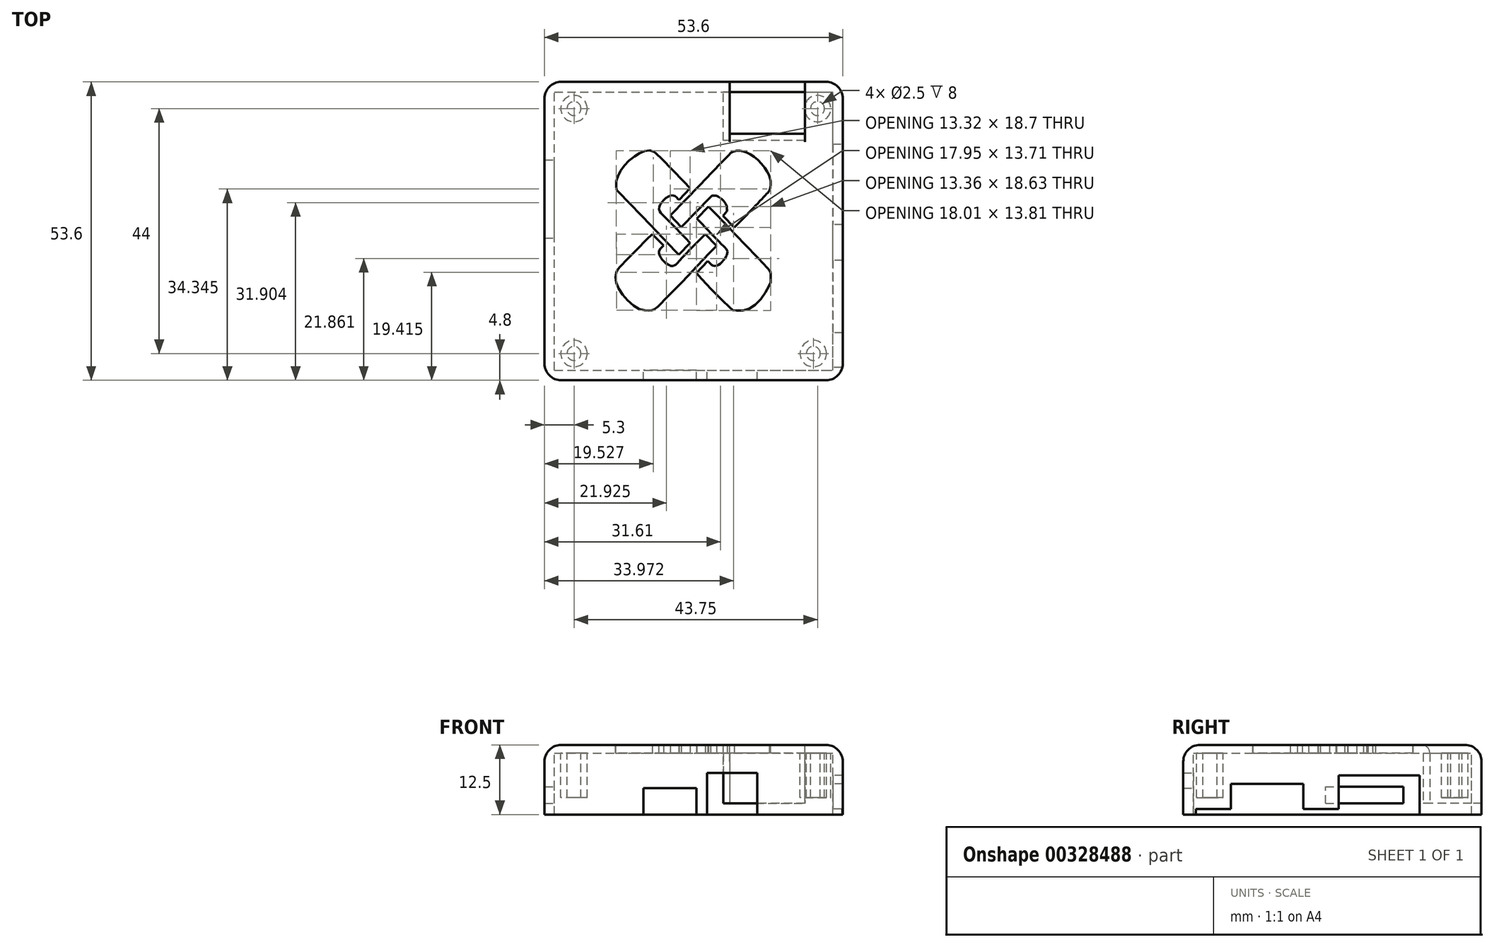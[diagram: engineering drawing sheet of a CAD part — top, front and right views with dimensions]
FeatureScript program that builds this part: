
annotation { "Feature Type Name" : "Feature", "Feature Type Description" : "" }
export const myFeature = defineFeature(function(context is Context, id is Id, definition is map)
    precondition{}
    {
        {
            var Q0;
            Q0=qCreatedBy(makeId("Top.planeOp"),FACE);
            var sketch = newSketch(context, id + "F0", { "sketchPlane" : qUnion([Q0])});
            skPoint(sketch, "E0.middle", {"position": v(0, 0) * mm});
            skLineSegment(sketch, "E1.bottom", {"start": v(-25, -25) * mm, "end": v(25, -25) * mm});
            skLineSegment(sketch, "E1.top", {"start": v(-25, 25) * mm, "end": v(25, 25) * mm});
            skLineSegment(sketch, "E1.left", {"start": v(-25, -25) * mm, "end": v(-25, 25) * mm});
            skLineSegment(sketch, "E1.right", {"start": v(25, -25) * mm, "end": v(25, 25) * mm});
            skLineSegment(sketch, "E2.0", {"start": v(-26.8, 26.8) * mm, "end": v(26.8, 26.8) * mm});
            skLineSegment(sketch, "E2.1", {"start": v(-26.8, -26.8) * mm, "end": v(-26.8, 26.8) * mm});
            skLineSegment(sketch, "E2.2", {"start": v(-26.8, -26.8) * mm, "end": v(26.8, -26.8) * mm});
            skLineSegment(sketch, "E2.3", {"start": v(26.8, -26.8) * mm, "end": v(26.8, 26.8) * mm});
            skLineSegment(sketch, "E3.bottom", {"start": v(-21.5, -22) * mm, "end": v(21.5, -22) * mm, "construction": true});
            skLineSegment(sketch, "E3.top", {"start": v(-21.5, 22) * mm, "end": v(21.5, 22) * mm, "construction": true});
            skLineSegment(sketch, "E3.left", {"start": v(-21.5, -22) * mm, "end": v(-21.5, 22) * mm, "construction": true});
            skLineSegment(sketch, "E3.right", {"start": v(21.5, -22) * mm, "end": v(21.5, 22) * mm, "construction": true});
            skLineSegment(sketch, "E4", {"start": v(21.5, 22) * mm, "end": v(22.25, 22) * mm, "construction": true});
            skCircle(sketch, "E5", {"center": v(22.25, 22) * mm, "radius": 1.25 * mm});
            skCircle(sketch, "E6", {"center": v(-21.5, 22) * mm, "radius": 1.25 * mm});
            skCircle(sketch, "E7", {"center": v(-21.5, -22) * mm, "radius": 1.25 * mm});
            skCircle(sketch, "E8", {"center": v(21.5, -22) * mm, "radius": 1.25 * mm});
            skCircle(sketch, "E9", {"center": v(-21.5, 22) * mm, "radius": 2.38 * mm});
            skCircle(sketch, "E10", {"center": v(22.25, 22) * mm, "radius": 2.38 * mm});
            skCircle(sketch, "E11", {"center": v(21.5, -22) * mm, "radius": 2.38 * mm});
            skCircle(sketch, "E12", {"center": v(-21.5, -22) * mm, "radius": 2.38 * mm});
            skSolve(sketch);
        }
        {
            var Q0;
            Q0=makeQuery(id+"F0.imprint","IMPRINT",FACE,{"disambiguationData":[TD([[makeQuery(id+"F0.imprint","IMPRINT",EDGE,{"derivedFrom":sQuery(id+"F0.wireOp",EDGE,"E1.bottom")}),1.0]])]});
            var Q1;
            Q1=makeQuery(id+"F0.imprint","IMPRINT",FACE,{"disambiguationData":[TD([[makeQuery(id+"F0.imprint","IMPRINT",EDGE,{"derivedFrom":sQuery(id+"F0.wireOp",EDGE,"E6")}),1.0]])]});
            var Q2;
            Q2=makeQuery(id+"F0.imprint","IMPRINT",FACE,{"disambiguationData":[TD([[makeQuery(id+"F0.imprint","IMPRINT",EDGE,{"derivedFrom":sQuery(id+"F0.wireOp",EDGE,"E5")}),1.0]])]});
            var Q3;
            Q3=makeQuery(id+"F0.imprint","IMPRINT",FACE,{"disambiguationData":[TD([[makeQuery(id+"F0.imprint","IMPRINT",EDGE,{"derivedFrom":sQuery(id+"F0.wireOp",EDGE,"E8")}),1.0]])]});
            var Q4;
            Q4=makeQuery(id+"F0.imprint","IMPRINT",FACE,{"disambiguationData":[TD([[makeQuery(id+"F0.imprint","IMPRINT",EDGE,{"derivedFrom":sQuery(id+"F0.wireOp",EDGE,"E7")}),1.0]])]});
            extrude(context, id + "F1", {"entities" : qUnion([Q0, Q1, Q2, Q3, Q4]), "depth" : 1.5 * mm});
        }
        {
            var Q0;
            Q0=makeQuery(id+"F0.imprint","IMPRINT",FACE,{"disambiguationData":[TD([[makeQuery(id+"F0.imprint","IMPRINT",EDGE,{"derivedFrom":sQuery(id+"F0.wireOp",EDGE,"E6")}),-1.0]])]});
            var Q1;
            Q1=makeQuery(id+"F0.imprint","IMPRINT",FACE,{"disambiguationData":[TD([[makeQuery(id+"F0.imprint","IMPRINT",EDGE,{"derivedFrom":sQuery(id+"F0.wireOp",EDGE,"E5")}),-1.0]])]});
            var Q2;
            Q2=makeQuery(id+"F0.imprint","IMPRINT",FACE,{"disambiguationData":[TD([[makeQuery(id+"F0.imprint","IMPRINT",EDGE,{"derivedFrom":sQuery(id+"F0.wireOp",EDGE,"E8")}),-1.0]])]});
            var Q3;
            Q3=makeQuery(id+"F0.imprint","IMPRINT",FACE,{"disambiguationData":[TD([[makeQuery(id+"F0.imprint","IMPRINT",EDGE,{"derivedFrom":sQuery(id+"F0.wireOp",EDGE,"E7")}),-1.0]])]});
            var Q4;
            Q4=makeQuery(id+"F1.opExtrude","CAP_FACE",FACE,{"disambiguationData":[OSD([sQuery(id+"F0.wireOp",EDGE,"E1.bottom"),sQuery(id+"F0.wireOp",EDGE,"E1.top"),sQuery(id+"F0.wireOp",EDGE,"E1.left"),sQuery(id+"F0.wireOp",EDGE,"E1.right"),sQuery(id+"F0.wireOp",EDGE,"E9"),sQuery(id+"F0.wireOp",EDGE,"E10"),sQuery(id+"F0.wireOp",EDGE,"E11"),sQuery(id+"F0.wireOp",EDGE,"E12")])],"isStart":false});
            extrude(context, id + "F2", {"entities" : qUnion([Q0, Q1, Q2, Q3]), "operationType" : NewBodyOperationType.ADD, "oppositeDirection" : true, "depth" : 8 * mm, "hasSecondDirection" : true, "secondDirectionOppositeDirection" : false, "secondDirectionBoundEntityFace" : qUnion([Q4]), "secondDirectionDepth" : 1.5 * mm});
        }
        {
            var Q0;
            Q0=makeQuery(id+"F0.imprint","IMPRINT",FACE,{"disambiguationData":[TD([[makeQuery(id+"F0.imprint","IMPRINT",EDGE,{"derivedFrom":sQuery(id+"F0.wireOp",EDGE,"E1.bottom")}),-1.0]])]});
            extrude(context, id + "F3", {"entities" : qUnion([Q0]), "operationType" : NewBodyOperationType.ADD, "oppositeDirection" : true, "depth" : 11 * mm, "hasSecondDirection" : true, "secondDirectionOppositeDirection" : false, "secondDirectionDepth" : 1.5 * mm});
        }
        {
            var Q0;
            Q0=qCreatedBy(makeId("Front.planeOp"),FACE);
            var sketch = newSketch(context, id + "F4", { "sketchPlane" : qUnion([Q0])});
            skLineSegment(sketch, "E13", {"start": v(0, 0) * mm, "end": v(0, -10) * mm, "construction": true});
            skLineSegment(sketch, "E14", {"start": v(0, -10) * mm, "end": v(-24.5, -10) * mm, "construction": true});
            skLineSegment(sketch, "E15", {"start": v(-24.5, -10) * mm, "end": v(-24.5, -7.25) * mm, "construction": true});
            skLineSegment(sketch, "E16", {"start": v(-24.5, -7.25) * mm, "end": v(-4.25, -7.25) * mm, "construction": true});
            skLineSegment(sketch, "E17.bottom", {"start": v(-9, -8.25) * mm, "end": v(0.5, -8.25) * mm});
            skLineSegment(sketch, "E17.top", {"start": v(-9, -6.25) * mm, "end": v(0.5, -6.25) * mm});
            skLineSegment(sketch, "E17.left", {"start": v(-9, -8.25) * mm, "end": v(-9, -6.25) * mm});
            skLineSegment(sketch, "E17.right", {"start": v(0.5, -8.25) * mm, "end": v(0.5, -6.25) * mm});
            skPoint(sketch, "E17.middle", {"position": v(-4.25, -7.25) * mm});
            skLineSegment(sketch, "E18", {"start": v(-24.5, -7.25) * mm, "end": v(-24.5, -6.15) * mm, "construction": true});
            skLineSegment(sketch, "E19", {"start": v(-24.5, -6.15) * mm, "end": v(6.9, -6.15) * mm, "construction": true});
            skLineSegment(sketch, "E20.bottom", {"start": v(11.4, -8.75) * mm, "end": v(2.4, -8.75) * mm});
            skLineSegment(sketch, "E20.top", {"start": v(11.4, -3.55) * mm, "end": v(2.4, -3.55) * mm});
            skLineSegment(sketch, "E20.left", {"start": v(11.4, -8.75) * mm, "end": v(11.4, -3.55) * mm});
            skLineSegment(sketch, "E20.right", {"start": v(2.4, -8.75) * mm, "end": v(2.4, -3.55) * mm});
            skPoint(sketch, "E20.middle", {"position": v(6.9, -6.15) * mm});
            skLineSegment(sketch, "E21", {"start": v(11.4, -8.75) * mm, "end": v(11.4, -11) * mm});
            skLineSegment(sketch, "E22", {"start": v(11.4, -11) * mm, "end": v(2.4, -11) * mm});
            skLineSegment(sketch, "E23", {"start": v(2.4, -11) * mm, "end": v(2.4, -8.75) * mm});
            skLineSegment(sketch, "E24", {"start": v(0.5, -8.25) * mm, "end": v(0.5, -11) * mm});
            skLineSegment(sketch, "E25", {"start": v(0.5, -11) * mm, "end": v(-9, -11) * mm});
            skLineSegment(sketch, "E26", {"start": v(-9, -11) * mm, "end": v(-9, -8.25) * mm});
            skLineSegment(sketch, "E27", {"start": v(2.4, -11.11) * mm, "end": v(2.4, -12.2) * mm});
            skSolve(sketch);
        }
        {
            var Q0;
            Q0 = qSketchRegion(id + "F4", true);
            extrude(context, id + "F5", {"entities" : qUnion([Q0]), "operationType" : NewBodyOperationType.REMOVE, "endBound" : BoundingType.THROUGH_ALL, "depth" : 25 * mm});
        }
        {
            var Q0;
            Q0=qCreatedBy(makeId("Right.planeOp"),FACE);
            var sketch = newSketch(context, id + "F6", { "sketchPlane" : qUnion([Q0])});
            skLineSegment(sketch, "E28", {"start": v(0, 0) * mm, "end": v(0, -10) * mm, "construction": true});
            skLineSegment(sketch, "E29", {"start": v(0, -10) * mm, "end": v(-24.5, -10) * mm});
            skLineSegment(sketch, "E30", {"start": v(-24.5, -10) * mm, "end": v(-24.5, -7) * mm, "construction": true});
            skLineSegment(sketch, "E31", {"start": v(-24.5, -7) * mm, "end": v(-11.75, -7) * mm, "construction": true});
            skLineSegment(sketch, "E32.bottom", {"start": v(-18.25, -8.5) * mm, "end": v(-5.25, -8.5) * mm});
            skLineSegment(sketch, "E32.top", {"start": v(-18.25, -5.5) * mm, "end": v(-5.25, -5.5) * mm});
            skLineSegment(sketch, "E32.left", {"start": v(-18.25, -8.5) * mm, "end": v(-18.25, -5.5) * mm});
            skLineSegment(sketch, "E32.right", {"start": v(-5.25, -8.5) * mm, "end": v(-5.25, -5.5) * mm});
            skPoint(sketch, "E32.middle", {"position": v(-11.75, -7) * mm});
            skLineSegment(sketch, "E33", {"start": v(0, -10) * mm, "end": v(8.4, -10) * mm, "construction": true});
            skLineSegment(sketch, "E34", {"start": v(8.4, -10) * mm, "end": v(8.4, -7) * mm, "construction": true});
            skLineSegment(sketch, "E35.bottom", {"start": v(1.14, -10) * mm, "end": v(15.64, -10) * mm});
            skLineSegment(sketch, "E35.top", {"start": v(1.14, -4) * mm, "end": v(15.64, -4) * mm});
            skLineSegment(sketch, "E35.left", {"start": v(1.14, -10) * mm, "end": v(1.14, -4) * mm});
            skLineSegment(sketch, "E35.right", {"start": v(15.64, -10) * mm, "end": v(15.64, -4) * mm});
            skPoint(sketch, "E35.middle", {"position": v(8.4, -7) * mm});
            skLineSegment(sketch, "E36", {"start": v(-18.25, -8.5) * mm, "end": v(-18.25, -11.13) * mm});
            skLineSegment(sketch, "E37", {"start": v(-18.25, -11.13) * mm, "end": v(-5.25, -11.13) * mm});
            skLineSegment(sketch, "E38", {"start": v(-5.25, -11.13) * mm, "end": v(-5.25, -8.5) * mm});
            skLineSegment(sketch, "E39", {"start": v(1.14, -10) * mm, "end": v(1.14, -11.13) * mm});
            skLineSegment(sketch, "E40", {"start": v(1.14, -11.13) * mm, "end": v(15.64, -11.13) * mm});
            skLineSegment(sketch, "E41", {"start": v(15.64, -11.13) * mm, "end": v(15.64, -10) * mm});
            skLineSegment(sketch, "E42", {"start": v(-24.5, -10) * mm, "end": v(-24.5, -11.13) * mm});
            skLineSegment(sketch, "E43", {"start": v(-24.5, -11.13) * mm, "end": v(-18.25, -11.13) * mm});
            skLineSegment(sketch, "E44", {"start": v(0, -10) * mm, "end": v(0, -11.13) * mm});
            skLineSegment(sketch, "E45", {"start": v(0, -11.13) * mm, "end": v(-5.25, -11.13) * mm});
            skLineSegment(sketch, "E46", {"start": v(0, -10) * mm, "end": v(1.14, -10) * mm});
            skLineSegment(sketch, "E47", {"start": v(0, -11.13) * mm, "end": v(1.14, -11.13) * mm});
            skSolve(sketch);
        }
        {
            var Q0;
            Q0 = qSketchRegion(id + "F6", true);
            extrude(context, id + "F7", {"entities" : qUnion([Q0]), "operationType" : NewBodyOperationType.REMOVE, "endBound" : BoundingType.THROUGH_ALL, "depth" : 25 * mm});
        }
        {
            var Q0;
            Q0=qCreatedBy(makeId("Right.planeOp"),FACE);
            cPlane(context, id + "F8", {"entities" : qUnion([Q0]), "cplaneType" : CPlaneType.OFFSET, "offset" : 6.5 * mm, "width" : 150 * mm, "height" : 150 * mm});
        }
        {
            var Q0;
            Q0=qCreatedBy(id+"F8.planeOp",FACE);
            var sketch = newSketch(context, id + "F9", { "sketchPlane" : qUnion([Q0])});
            skLineSegment(sketch, "E48", {"start": v(0, 0) * mm, "end": v(26.8, 0) * mm, "construction": true});
            skLineSegment(sketch, "E49.bottom", {"start": v(26.8, 0) * mm, "end": v(16.3, 0) * mm});
            skLineSegment(sketch, "E49.top", {"start": v(26.8, -9) * mm, "end": v(16.3, -9) * mm});
            skLineSegment(sketch, "E49.left", {"start": v(26.8, 0) * mm, "end": v(26.8, -9) * mm});
            skLineSegment(sketch, "E49.right", {"start": v(16.3, 0) * mm, "end": v(16.3, -9) * mm});
            skLineSegment(sketch, "E50.1", {"start": v(17.5, 0) * mm, "end": v(17.5, -5.8) * mm});
            skLineSegment(sketch, "E51", {"start": v(17.5, -5.8) * mm, "end": v(17.5, -9) * mm});
            skLineSegment(sketch, "E52", {"start": v(16.3, 0) * mm, "end": v(16.3, 1.5) * mm});
            skLineSegment(sketch, "E53", {"start": v(16.3, 1.5) * mm, "end": v(26.8, 1.5) * mm});
            skLineSegment(sketch, "E54", {"start": v(26.8, 1.5) * mm, "end": v(26.8, 0) * mm});
            skLineSegment(sketch, "E55", {"start": v(17.5, 0) * mm, "end": v(17.5, 1.5) * mm});
            skSolve(sketch);
        }
        {
            var Q0;
            Q0 = qSketchRegion(id + "F9", true);
            extrude(context, id + "F10", {"entities" : qUnion([Q0]), "operationType" : NewBodyOperationType.REMOVE, "depth" : 13.5 * mm});
        }
        {
            var Q0;
            {var subQ0=sQuery(id+"F9.wireOp",EDGE,"E49.right");Q0=makeQuery(id+"F9.imprint","IMPRINT",FACE,{"disambiguationData":[TD([[makeQuery(id+"F9.imprint","IMPRINT",EDGE,{"derivedFrom":subQ0}),1.0]])]});}
            var Q1;
            {var subQ0=sQuery(id+"F9.wireOp",EDGE,"E52");Q1=makeQuery(id+"F9.imprint","IMPRINT",FACE,{"disambiguationData":[TD([[makeQuery(id+"F9.imprint","IMPRINT",EDGE,{"derivedFrom":subQ0}),-1.0]])]});}
            var Q2;
            Q2=makeQuery(id+"F3.opExtrude","SWEPT_FACE",FACE,{"disambiguationData":[OSD([sQuery(id+"F0.wireOp",EDGE,"E2.3")])]});
            extrude(context, id + "F11", {"entities" : qUnion([Q0, Q1]), "operationType" : NewBodyOperationType.ADD, "endBoundEntityFace" : qUnion([Q2]), "depth" : 13.5 * mm});
        }
        {
            var Q0;
            Q0 = qSketchRegion(id + "F9", true);
            extrude(context, id + "F12", {"entities" : qUnion([Q0]), "operationType" : NewBodyOperationType.ADD, "oppositeDirection" : true, "depth" : 1.2 * mm});
        }
        {
            var Q0;
            {var subQ6=sQuery(id+"F0.wireOp",EDGE,"E2.3");var subQ9=sQuery(id+"F0.wireOp",EDGE,"E2.0");Q0=makeQuery(id+"F10.boolean.opBoolean","SPLIT",EDGE,{"disambiguationData":[TD([makeQuery(id+"F3.opExtrude","SWEPT_FACE",FACE,{"disambiguationData":[OSD([subQ6])]})])],"derivedFrom":makeQuery(id+"F3.opExtrude","CAP_EDGE",EDGE,{"disambiguationData":[OSD([subQ9])],"isStart":true})});}
            var Q1;
            {var subQ8=sQuery(id+"F0.wireOp",EDGE,"E2.0");var subQ13=sQuery(id+"F0.wireOp",EDGE,"E2.1");Q1=makeQuery(id+"F10.boolean.opBoolean","SPLIT",EDGE,{"disambiguationData":[TD([makeQuery(id+"F3.opExtrude","SWEPT_FACE",FACE,{"disambiguationData":[OSD([subQ13])]})])],"derivedFrom":makeQuery(id+"F3.opExtrude","CAP_EDGE",EDGE,{"disambiguationData":[OSD([subQ8])],"isStart":true})});}
            var Q2;
            {var subQ4=sQuery(id+"F9.wireOp",EDGE,"E49.right");var subQ5=sQuery(id+"F9.wireOp",EDGE,"E49.left");var subQ6=sQuery(id+"F9.wireOp",EDGE,"E49.top");var subQ7=sQuery(id+"F9.wireOp",EDGE,"E49.bottom");var subQ16=sQuery(id+"F9.wireOp",EDGE,"E50.1");Q2=makeQuery(id+"F11.boolean.opBoolean","SPLIT",EDGE,{"disambiguationData":[TD([makeQuery(id+"F10.boolean.opBoolean","COPY",FACE,{"derivedFrom":makeQuery(id+"F10.opExtrude","CAP_FACE",FACE,{"disambiguationData":[OSD([subQ7,subQ6,subQ5,subQ4])],"isStart":true})})])],"derivedFrom":makeQuery(id+"F11.opExtrude","SWEPT_EDGE",EDGE,{"disambiguationData":[OSD([subQ7,subQ16])]})});}
            var Q3;
            Q3=makeQuery(id+"F10.boolean.opBoolean","COPY",EDGE,{"derivedFrom":makeQuery(id+"F10.opExtrude","CAP_EDGE",EDGE,{"disambiguationData":[OSD([sQuery(id+"F9.wireOp",EDGE,"E49.bottom")])],"isStart":true})});
            var Q4;
            Q4=makeQuery(id+"F3.opExtrude","CAP_EDGE",EDGE,{"disambiguationData":[OSD([sQuery(id+"F0.wireOp",EDGE,"E2.1")])],"isStart":true});
            var Q5;
            Q5=makeQuery(id+"F3.opExtrude","CAP_EDGE",EDGE,{"disambiguationData":[OSD([sQuery(id+"F0.wireOp",EDGE,"E2.2")])],"isStart":true});
            var Q6;
            Q6=makeQuery(id+"F3.opExtrude","SWEPT_EDGE",EDGE,{"disambiguationData":[OSD([sQuery(id+"F0.wireOp",EDGE,"E2.1"),sQuery(id+"F0.wireOp",EDGE,"E2.2")])]});
            var Q7;
            Q7=makeQuery(id+"F10.boolean.opBoolean","COPY",EDGE,{"derivedFrom":makeQuery(id+"F10.opExtrude","CAP_EDGE",EDGE,{"disambiguationData":[OSD([sQuery(id+"F9.wireOp",EDGE,"E49.left")])],"isStart":false})});
            var Q8;
            Q8=makeQuery(id+"F3.opExtrude","SWEPT_EDGE",EDGE,{"disambiguationData":[OSD([sQuery(id+"F0.wireOp",EDGE,"E2.0"),sQuery(id+"F0.wireOp",EDGE,"E2.3")])]});
            var Q9;
            {var subQ6=sQuery(id+"F0.wireOp",EDGE,"E2.3");var subQ13=sQuery(id+"F0.wireOp",EDGE,"E2.2");Q9=makeQuery(id+"F11.boolean.opBoolean","SPLIT",EDGE,{"disambiguationData":[TD([makeQuery(id+"F3.opExtrude","SWEPT_FACE",FACE,{"disambiguationData":[OSD([subQ13])]})])],"derivedFrom":makeQuery(id+"F3.opExtrude","CAP_EDGE",EDGE,{"disambiguationData":[OSD([subQ6])],"isStart":true})});}
            var Q10;
            Q10=makeQuery(id+"F3.opExtrude","SWEPT_EDGE",EDGE,{"disambiguationData":[OSD([sQuery(id+"F0.wireOp",EDGE,"E2.2"),sQuery(id+"F0.wireOp",EDGE,"E2.3")])]});
            var Q11;
            Q11=makeQuery(id+"F3.opExtrude","SWEPT_EDGE",EDGE,{"disambiguationData":[OSD([sQuery(id+"F0.wireOp",EDGE,"E2.0"),sQuery(id+"F0.wireOp",EDGE,"E2.1")])]});
            fillet(context, id + "F13", {"entities" : qUnion([Q0, Q1, Q2, Q3, Q4, Q5, Q6, Q7, Q8, Q9, Q10, Q11]), "radius" : 3 * mm, "tangentPropagation" : true, "allowEdgeOverflow" : false});
        }
        {
            var Q0;
            Q0=makeQuery(id+"F11.opExtrude","SWEPT_EDGE",EDGE,{"disambiguationData":[OSD([sQuery(id+"F9.wireOp",EDGE,"E53"),sQuery(id+"F9.wireOp",EDGE,"E55")])]});
            fillet(context, id + "F14", {"entities" : qUnion([Q0]), "radius" : 1.5 * mm, "tangentPropagation" : true, "allowEdgeOverflow" : false});
        }
        {
            var Q0;
            Q0=qCreatedBy(makeId("Right.planeOp"),FACE);
            var sketch = newSketch(context, id + "F15", { "sketchPlane" : qUnion([Q0])});
            skLineSegment(sketch, "E56", {"start": v(0, 0) * mm, "end": v(0, -9) * mm, "construction": true});
            skLineSegment(sketch, "E57.bottom", {"start": v(24.5, -10) * mm, "end": v(-24.5, -10) * mm});
            skLineSegment(sketch, "E57.top", {"start": v(24.5, -8) * mm, "end": v(-24.5, -8) * mm});
            skLineSegment(sketch, "E57.left", {"start": v(24.5, -10) * mm, "end": v(24.5, -8) * mm});
            skLineSegment(sketch, "E57.right", {"start": v(-24.5, -10) * mm, "end": v(-24.5, -8) * mm});
            skPoint(sketch, "E57.middle", {"position": v(0, -9) * mm});
            skLineSegment(sketch, "E58", {"start": v(0, -9) * mm, "end": v(5.75, -9) * mm, "construction": true});
            skLineSegment(sketch, "E59", {"start": v(5.75, -9) * mm, "end": v(5.75, -8) * mm, "construction": true});
            skLineSegment(sketch, "E60.bottom", {"start": v(-1.25, -10) * mm, "end": v(12.75, -10) * mm});
            skLineSegment(sketch, "E60.top", {"start": v(-1.25, -6) * mm, "end": v(12.75, -6) * mm});
            skLineSegment(sketch, "E60.left", {"start": v(-1.25, -10) * mm, "end": v(-1.25, -6) * mm});
            skLineSegment(sketch, "E60.right", {"start": v(12.75, -10) * mm, "end": v(12.75, -6) * mm});
            skPoint(sketch, "E60.middle", {"position": v(5.75, -8) * mm});
            skLineSegment(sketch, "E61", {"start": v(0, -9) * mm, "end": v(-24.5, -9) * mm});
            skLineSegment(sketch, "E62", {"start": v(0, -9) * mm, "end": v(24.5, -9) * mm});
            skLineSegment(sketch, "E63", {"start": v(24.5, -10) * mm, "end": v(24.5, -11.04) * mm});
            skLineSegment(sketch, "E64", {"start": v(24.5, -11.04) * mm, "end": v(-24.5, -11.04) * mm});
            skLineSegment(sketch, "E65", {"start": v(-24.5, -11.04) * mm, "end": v(-24.5, -10) * mm});
            skSolve(sketch);
        }
        {
            var Q0;
            {var subQ5=sQuery(id+"F15.wireOp",EDGE,"E60.top");Q0=makeQuery(id+"F15.imprint","IMPRINT",FACE,{"disambiguationData":[TD([[makeQuery(id+"F15.imprint","IMPRINT",EDGE,{"derivedFrom":subQ5}),-1.0]])]});}
            var Q1;
            {var subQ0=sQuery(id+"F15.wireOp",EDGE,"E60.right");var subQ1=sQuery(id+"F15.wireOp",EDGE,"E57.top");var subQ2=makeQuery(id+"F15.imprint","INTERSECT",VERTEX,{"derivedFrom":[subQ1,subQ0]});Q1=makeQuery(id+"F15.imprint","IMPRINT",FACE,{"disambiguationData":[TD([[makeQuery(id+"F15.imprint","IMPRINT",EDGE,{"disambiguationData":[TD([[subQ2,-1.0]])],"derivedFrom":subQ1}),1.0]])]});}
            var Q2;
            {var subQ5=sQuery(id+"F15.wireOp",EDGE,"E60.bottom");Q2=makeQuery(id+"F15.imprint","IMPRINT",FACE,{"disambiguationData":[TD([[makeQuery(id+"F15.imprint","IMPRINT",EDGE,{"derivedFrom":subQ5}),1.0]])]});}
            var Q3;
            {var subQ0=sQuery(id+"F15.wireOp",EDGE,"E60.bottom");Q3=makeQuery(id+"F15.imprint","IMPRINT",FACE,{"disambiguationData":[TD([[makeQuery(id+"F15.imprint","IMPRINT",EDGE,{"derivedFrom":subQ0}),-1.0]])]});}
            extrude(context, id + "F16", {"entities" : qUnion([Q0, Q1, Q2, Q3]), "operationType" : NewBodyOperationType.REMOVE, "endBound" : BoundingType.THROUGH_ALL, "oppositeDirection" : true, "depth" : 25 * mm});
        }
        {
            var Q0;
            Q0=qCreatedBy(makeId("Top.planeOp"),FACE);
            var sketch = newSketch(context, id + "F17", { "sketchPlane" : qUnion([Q0])});
            skLineSegment(sketch, "E66", {"start": v(-4.34, 2.65) * mm, "end": v(-2.39, 0.57) * mm});
            skLineSegment(sketch, "E67", {"start": v(-2.39, 0.57) * mm, "end": v(3.07, 6.13) * mm});
            skFitSpline(sketch, "E68", {"points": [v(3.07, 6.13) * mm, v(3.32, 6.34) * mm, v(3.67, 6.39) * mm, v(4, 6.37) * mm, v(4.45, 6.17) * mm, v(4.85, 5.91) * mm, v(5.24, 5.57) * mm, v(5.67, 5) * mm, v(5.96, 4.45) * mm, v(6, 3.91) * mm, v(5.97, 3.58) * mm, v(5.24, 2.72) * mm, v(5.18, 2.64) * mm, v(5.18, 2.58) * mm, v(5.61, 2.13) * mm, v(7.06, 0.63) * mm, v(7.16, 0.57) * mm, v(7.26, 0.62) * mm, v(13.53, 7.13) * mm, v(13.59, 7.2) * mm, v(13.6, 7.27) * mm], "startDerivative": vector(5.99, 6.43) * mm, "endDerivative": vector(1.04, 4.5) * mm});
            skFitSpline(sketch, "E69", {"points": [v(-4.34, 2.65) * mm, v(6.64, 14) * mm, v(6.71, 14.08) * mm, v(7.22, 14.32) * mm, v(8.06, 14.45) * mm, v(8.88, 14.33) * mm, v(9.67, 14.06) * mm, v(10.72, 13.42) * mm, v(12.05, 12.24) * mm, v(13.07, 10.93) * mm, v(13.56, 10.02) * mm, v(13.75, 9.3) * mm, v(13.83, 8.8) * mm, v(13.82, 7.88) * mm, v(13.59, 7.2) * mm], "startDerivative": vector(63.12, 65.17) * mm, "endDerivative": vector(-5.23, -11.69) * mm});
            skFitSpline(sketch, "E70", {"points": [v(2.42, 4.55) * mm, v(13.55, -6.99) * mm, v(13.62, -7.1) * mm, v(13.77, -7.32) * mm, v(13.84, -7.83) * mm, v(13.85, -8.83) * mm, v(13.77, -9.37) * mm, v(12.05, -12.2) * mm, v(9.1, -14.24) * mm, v(7.08, -14.22) * mm, v(6.85, -14.1) * mm, v(0.5, -7.57) * mm, v(0.43, -7.43) * mm, v(0.47, -7.3) * mm, v(2.28, -5.38) * mm, v(2.4, -5.32) * mm, v(2.5, -5.36) * mm, v(3.22, -6.08) * mm, v(3.52, -6.25) * mm, v(4.14, -6.21) * mm, v(4.55, -6) * mm, v(5.26, -5.4) * mm, v(5.8, -4.63) * mm, v(5.96, -4.32) * mm, v(6.05, -3.85) * mm, v(5.94, -3.32) * mm, v(5.24, -2.6) * mm, v(5.17, -2.53) * mm, v(0.46, 2.3) * mm, v(0.43, 2.35) * mm, v(0.4, 2.44) * mm, v(0.48, 2.55) * mm, v(2.4, 4.54) * mm, v(2.4, 4.55) * mm, v(2.42, 4.55) * mm]});
            skFitSpline(sketch, "E71", {"points": [v(2.24, -0.38) * mm, v(4.22, -2.4) * mm, v(4.25, -2.44) * mm, v(4.23, -2.5) * mm, v(4.13, -2.6) * mm, v(-6.8, -13.9) * mm, v(-7.2, -14.1) * mm, v(-7.58, -14.22) * mm, v(-8.26, -14.24) * mm, v(-9.63, -14.06) * mm, v(-12.07, -12.25) * mm, v(-13.78, -9.7) * mm, v(-14.01, -7.96) * mm, v(-13.72, -7.03) * mm, v(-12.94, -6.11) * mm, v(-7.42, -0.5) * mm, v(-7.33, -0.45) * mm, v(-7.25, -0.46) * mm, v(-7.2, -0.51) * mm, v(-5.41, -2.33) * mm, v(-5.37, -2.4) * mm, v(-5.37, -2.49) * mm, v(-5.42, -2.57) * mm, v(-6.15, -3.44) * mm, v(-6.12, -4.36) * mm, v(-5.46, -5.35) * mm, v(-4.57, -6.04) * mm, v(-3.94, -6.27) * mm, v(-3.34, -6.12) * mm, v(-2.75, -5.54) * mm, v(2.2, -0.4) * mm], "startDerivative": vector(52.2, -53.28) * mm, "endDerivative": vector(75.14, 76.72) * mm});
            skLineSegment(sketch, "E72", {"start": v(2.24, -0.38) * mm, "end": v(2.2, -0.4) * mm});
            skFitSpline(sketch, "E73", {"points": [v(-0.5, -2.34) * mm, v(-2.37, -4.27) * mm, v(-2.52, -4.32) * mm, v(-2.65, -4.25) * mm, v(-4.21, -2.62) * mm, v(-13.74, 7.27) * mm, v(-13.83, 7.37) * mm, v(-13.93, 7.9) * mm, v(-13.84, 9.22) * mm, v(-13.28, 10.58) * mm, v(-11.98, 12.3) * mm, v(-10.13, 13.75) * mm, v(-8.83, 14.38) * mm, v(-7.5, 14.42) * mm, v(-6.91, 14.1) * mm, v(-6.42, 13.64) * mm, v(-0.59, 7.67) * mm, v(-0.54, 7.62) * mm, v(-0.54, 7.57) * mm, v(-0.57, 7.51) * mm, v(-2.39, 5.6) * mm, v(-2.47, 5.53) * mm, v(-2.58, 5.55) * mm, v(-2.68, 5.63) * mm, v(-3.28, 6.22) * mm, v(-3.7, 6.39) * mm, v(-4.3, 6.33) * mm, v(-5.42, 5.52) * mm, v(-6.16, 4.4) * mm, v(-6.13, 3.6) * mm, v(-5.2, 2.53) * mm, v(-0.5, -2.3) * mm], "startDerivative": vector(-49.13, -53.12) * mm, "endDerivative": vector(71.13, -74.32) * mm});
            skLineSegment(sketch, "E74", {"start": v(-0.5, -2.3) * mm, "end": v(-0.5, -2.34) * mm});
            skLineSegment(sketch, "E75", {"start": v(-0.62, -2.18) * mm, "end": v(-2.65, -4.25) * mm});
            skLineSegment(sketch, "E76", {"start": v(-2.24, 0.73) * mm, "end": v(-4.2, 2.8) * mm});
            skLineSegment(sketch, "E77", {"start": v(2.07, -0.54) * mm, "end": v(4.1, -2.63) * mm});
            skLineSegment(sketch, "E78", {"start": v(0.56, 2.2) * mm, "end": v(2.63, 4.38) * mm});
            skLineSegment(sketch, "E79", {"start": v(2.56, -5.4) * mm, "end": v(0.5, -7.57) * mm});
            skLineSegment(sketch, "E80", {"start": v(-5.42, -2.57) * mm, "end": v(-7.45, -0.53) * mm});
            skLineSegment(sketch, "E81", {"start": v(-2.62, 5.57) * mm, "end": v(-0.61, 7.7) * mm});
            skLineSegment(sketch, "E82", {"start": v(5.24, 2.72) * mm, "end": v(7.28, 0.64) * mm});
            skSolve(sketch);
        }
        {
            var Q0;
            {var subQ0=sQuery(id+"F17.wireOp",EDGE,"E78");Q0=makeQuery(id+"F17.imprint","IMPRINT",FACE,{"disambiguationData":[TD([[makeQuery(id+"F17.imprint","IMPRINT",EDGE,{"derivedFrom":subQ0}),-1.0]])]});}
            var Q1;
            {var subQ6=sQuery(id+"F17.wireOp",EDGE,"E76");Q1=makeQuery(id+"F17.imprint","IMPRINT",FACE,{"disambiguationData":[TD([[makeQuery(id+"F17.imprint","IMPRINT",EDGE,{"derivedFrom":subQ6}),-1.0]])]});}
            var Q2;
            {var subQ0=sQuery(id+"F17.wireOp",EDGE,"E75");Q2=makeQuery(id+"F17.imprint","IMPRINT",FACE,{"disambiguationData":[TD([[makeQuery(id+"F17.imprint","IMPRINT",EDGE,{"derivedFrom":subQ0}),-1.0]])]});}
            var Q3;
            {var subQ0=sQuery(id+"F17.wireOp",EDGE,"E77");Q3=makeQuery(id+"F17.imprint","IMPRINT",FACE,{"disambiguationData":[TD([[makeQuery(id+"F17.imprint","IMPRINT",EDGE,{"derivedFrom":subQ0}),-1.0]])]});}
            extrude(context, id + "F18", {"entities" : qUnion([Q0, Q1, Q2, Q3]), "operationType" : NewBodyOperationType.REMOVE, "endBound" : BoundingType.THROUGH_ALL, "depth" : 25 * mm});
        }
        {
            var Q0;
            {var subQ0=sQuery(id+"F17.wireOp",EDGE,"E78");Q0=makeQuery(id+"F17.imprint","IMPRINT",FACE,{"disambiguationData":[TD([[makeQuery(id+"F17.imprint","IMPRINT",EDGE,{"derivedFrom":subQ0}),-1.0]])]});}
            var Q1;
            {var subQ0=sQuery(id+"F17.wireOp",EDGE,"E77");Q1=makeQuery(id+"F17.imprint","IMPRINT",FACE,{"disambiguationData":[TD([[makeQuery(id+"F17.imprint","IMPRINT",EDGE,{"derivedFrom":subQ0}),-1.0]])]});}
            var Q2;
            {var subQ0=sQuery(id+"F17.wireOp",EDGE,"E75");Q2=makeQuery(id+"F17.imprint","IMPRINT",FACE,{"disambiguationData":[TD([[makeQuery(id+"F17.imprint","IMPRINT",EDGE,{"derivedFrom":subQ0}),-1.0]])]});}
            var Q3;
            {var subQ6=sQuery(id+"F17.wireOp",EDGE,"E76");Q3=makeQuery(id+"F17.imprint","IMPRINT",FACE,{"disambiguationData":[TD([[makeQuery(id+"F17.imprint","IMPRINT",EDGE,{"derivedFrom":subQ6}),-1.0]])]});}
            extrude(context, id + "F19", {"entities" : qUnion([Q0, Q1, Q2, Q3]), "depth" : 1.5 * mm});
        }
    });
